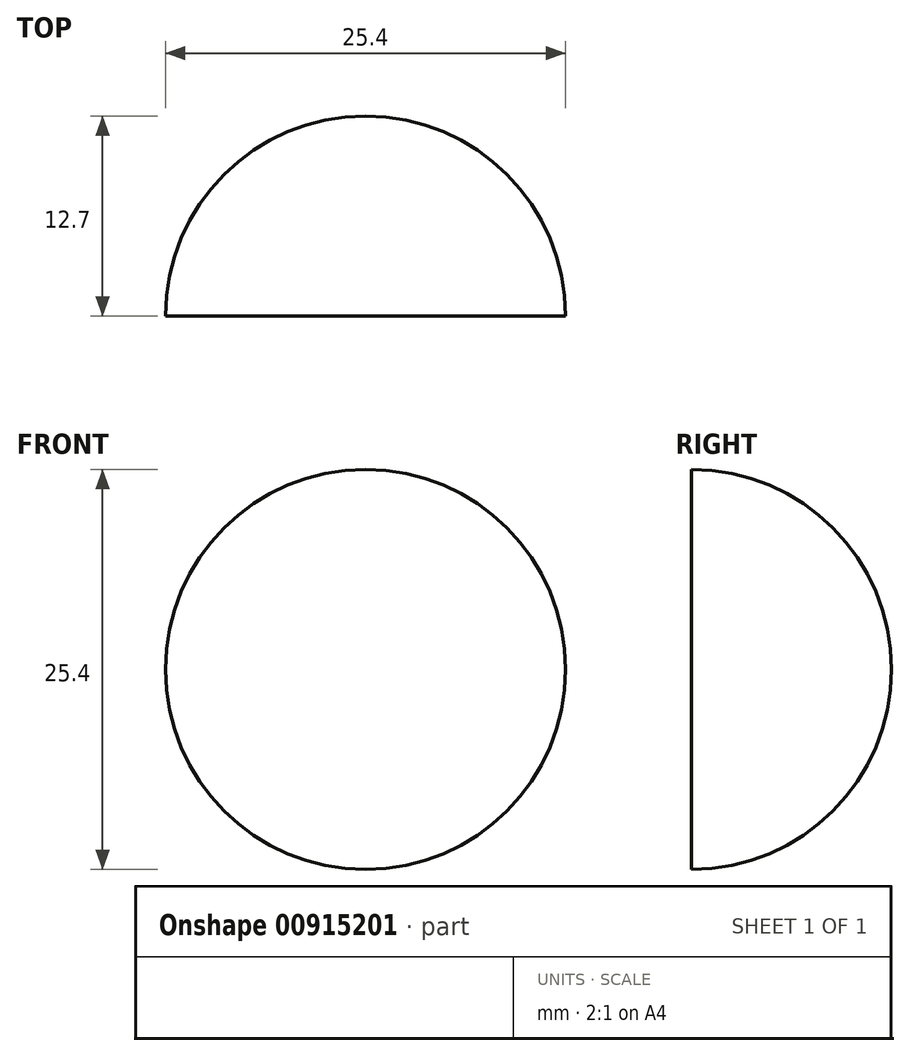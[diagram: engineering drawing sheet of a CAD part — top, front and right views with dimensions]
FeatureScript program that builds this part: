
annotation { "Feature Type Name" : "Feature", "Feature Type Description" : "" }
export const myFeature = defineFeature(function(context is Context, id is Id, definition is map)
    precondition{}
    {
        {
            var Q0;
            Q0=qCreatedBy(makeId("Front.planeOp"),FACE);
            var sketch = newSketch(context, id + "F0", { "sketchPlane" : qUnion([Q0])});
            skArc(sketch, "E0", {"start": v(0, 12.7) * mm, "mid": v(-12.7, 0) * mm, "end": v(0, -12.7) * mm});
            skLineSegment(sketch, "E1", {"start": v(0, 12.7) * mm, "end": v(0, 0) * mm});
            skLineSegment(sketch, "E2", {"start": v(0, 0) * mm, "end": v(0, -12.7) * mm});
            skSolve(sketch);
        }
        {
            var Q0;
            Q0=makeQuery(id+"F0.imprint","IMPRINT",FACE,{"disambiguationData":[TD([[makeQuery(id+"F0.imprint","IMPRINT",EDGE,{"derivedFrom":sQuery(id+"F0.wireOp",EDGE,"E0")}),1.0]])]});
            var Q1;
            Q1=sQuery(id+"F0.wireOp",EDGE,"E1");
            revolve(context, id + "F1", {"surfaceOperationType" : NewSurfaceOperationType.NEW, "entities" : qUnion([Q0]), "axis" : qUnion([Q1]), "revolveType" : RevolveType.ONE_DIRECTION, "angle" : 180 * degree});
        }
    });
